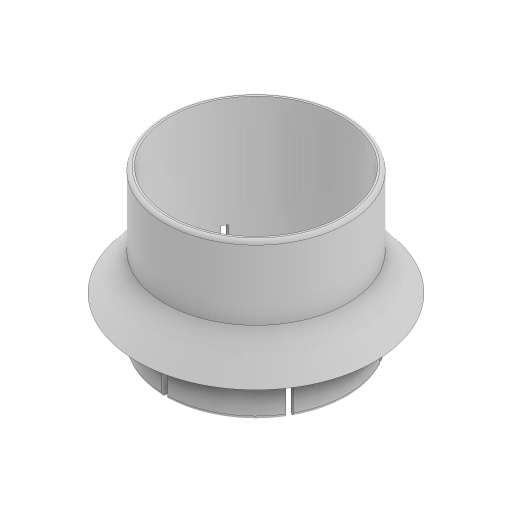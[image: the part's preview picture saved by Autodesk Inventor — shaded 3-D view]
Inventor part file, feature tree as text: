
AUTODESK INVENTOR PART (.ipt)
format: ipt  version: 2023 (Build 270158000, 158)  size: 200,704 bytes
history: native  units: mm
features: sketch x2, revolve x1, extrude x1, pattern_circular x1
ambient origin geometry x8: Origin, YZ Plane, XZ Plane, XY Plane, X Axis, Y Axis, Z Axis, Center Point
bodies: Solid1 (feature_tree)
feature tree (5):
  revolve  "Revolution1"  [1 undecoded]
  extrude  "Extrusion1"  Depth=3.0mm
  pattern_circular  "Circular Pattern1"  [2 undecoded]
  sketch  "Sketch1"  dims[d4=3.0mm d5=25.0mm]
  sketch  "Sketch2"  dims[d6=3.0mm d7=40.0mm d8=15.0mm d9=50.0mm d10=2.0mm d11=90.0deg d12=20.0mm d13=3.0mm d14=10.0mm d15=25.0mm d16=0.0mm d17=60.0mm d18=360.0deg]
note: 3 required parameter values undecoded (feature->parameter linkage not recoverable at this tier; creation-order binding heuristic only, values carry confidence <= 0.55)